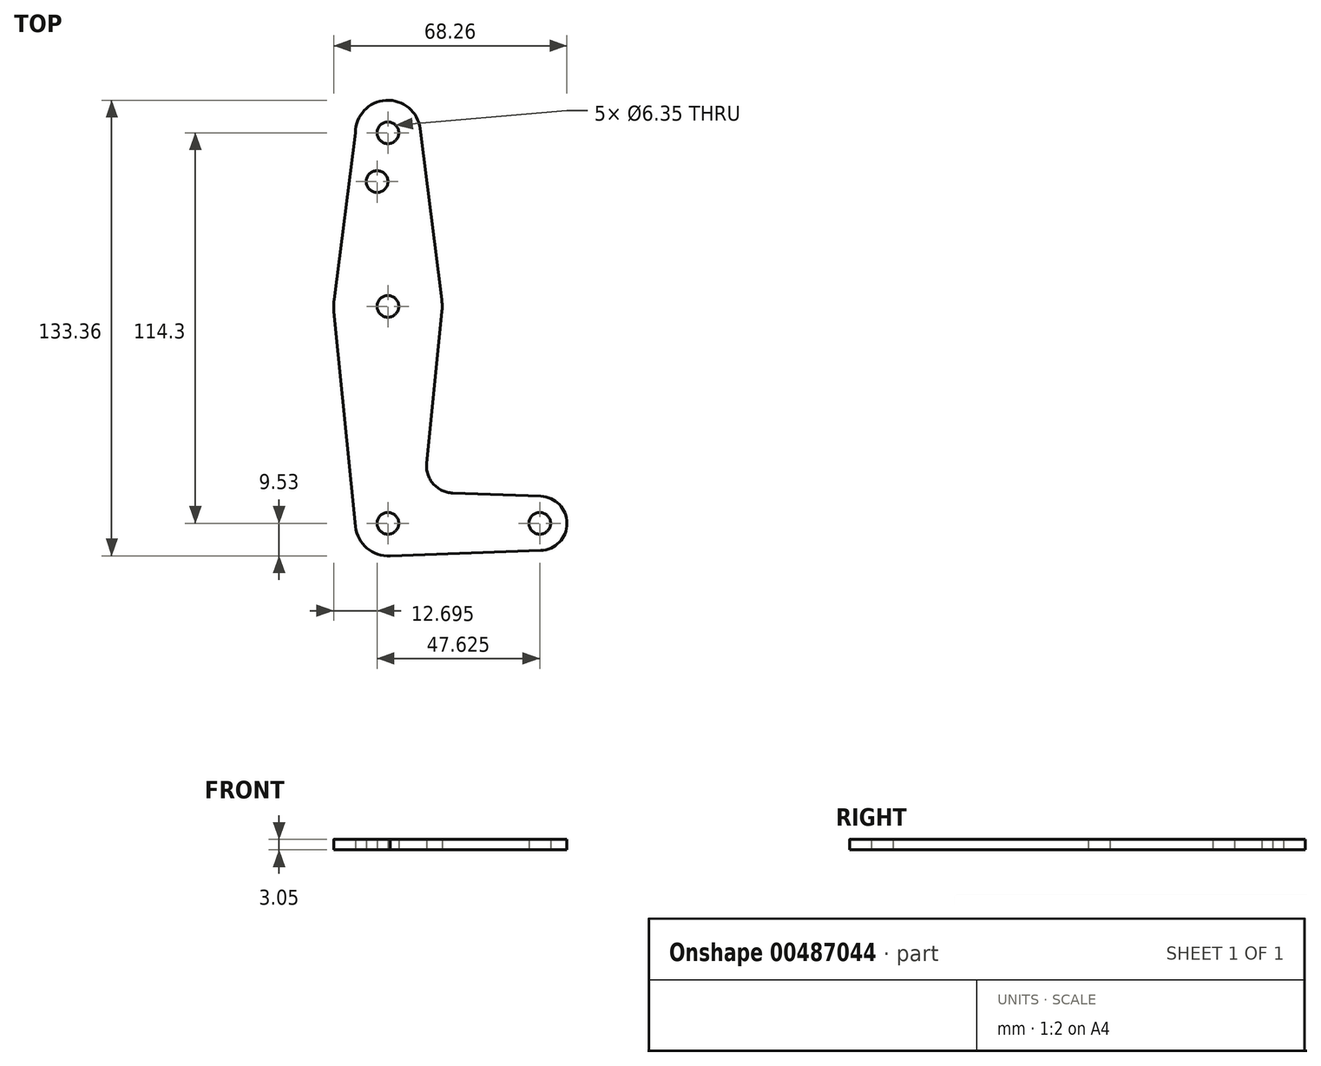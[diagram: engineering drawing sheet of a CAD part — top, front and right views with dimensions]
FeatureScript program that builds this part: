
annotation { "Feature Type Name" : "Feature", "Feature Type Description" : "" }
export const myFeature = defineFeature(function(context is Context, id is Id, definition is map)
    precondition{}
    {
        {
            var Q0;
            Q0=qCreatedBy(makeId("Top.planeOp"),FACE);
            var sketch = newSketch(context, id + "F0", { "sketchPlane" : qUnion([Q0])});
            skLineSegment(sketch, "E0", {"start": v(0, 0) * mm, "end": v(0, 114.3) * mm, "construction": true});
            skLineSegment(sketch, "E1", {"start": v(0, 0) * mm, "end": v(44.45, 0) * mm, "construction": true});
            skCircle(sketch, "E2", {"center": v(0, 0) * mm, "radius": 9.53 * mm});
            skCircle(sketch, "E3", {"center": v(0, 114.3) * mm, "radius": 9.53 * mm});
            skCircle(sketch, "E4", {"center": v(44.45, 0) * mm, "radius": 7.94 * mm});
            skCircle(sketch, "E5", {"center": v(0, 63.5) * mm, "radius": 15.88 * mm});
            skLineSegment(sketch, "E6", {"start": v(9.45, 115.5) * mm, "end": v(15.75, 65.48) * mm});
            skLineSegment(sketch, "E7", {"start": v(-9.53, 114.3) * mm, "end": v(-15.75, 65.5) * mm});
            skLineSegment(sketch, "E8", {"start": v(18.97, 8.85) * mm, "end": v(44.73, 7.93) * mm});
            skLineSegment(sketch, "E9", {"start": v(0, -9.53) * mm, "end": v(44.73, -7.93) * mm});
            skLineSegment(sketch, "E10", {"start": v(-15.8, 61.91) * mm, "end": v(-9.48, -0.95) * mm});
            skLineSegment(sketch, "E11", {"start": v(15.8, 61.91) * mm, "end": v(11.34, 17.6) * mm});
            skCircle(sketch, "E12", {"center": v(0, 114.3) * mm, "radius": 3.18 * mm});
            skCircle(sketch, "E13", {"center": v(-3.18, 100.03) * mm, "radius": 3.18 * mm});
            skCircle(sketch, "E14", {"center": v(0, 63.5) * mm, "radius": 3.18 * mm});
            skCircle(sketch, "E15", {"center": v(0, 0) * mm, "radius": 3.18 * mm});
            skCircle(sketch, "E16", {"center": v(44.45, 0) * mm, "radius": 3.17 * mm});
            skArc(sketch, "E17.filletArc", {"start": v(11.34, 17.6) * mm, "mid": v(13.26, 11.57) * mm, "end": v(18.97, 8.85) * mm});
            skSolve(sketch);
        }
        {
            var Q0;
            Q0 = qSketchRegion(id + "F0", true);
            extrude(context, id + "F1", {"entities" : qUnion([Q0]), "depth" : 3.05 * mm});
        }
    });
